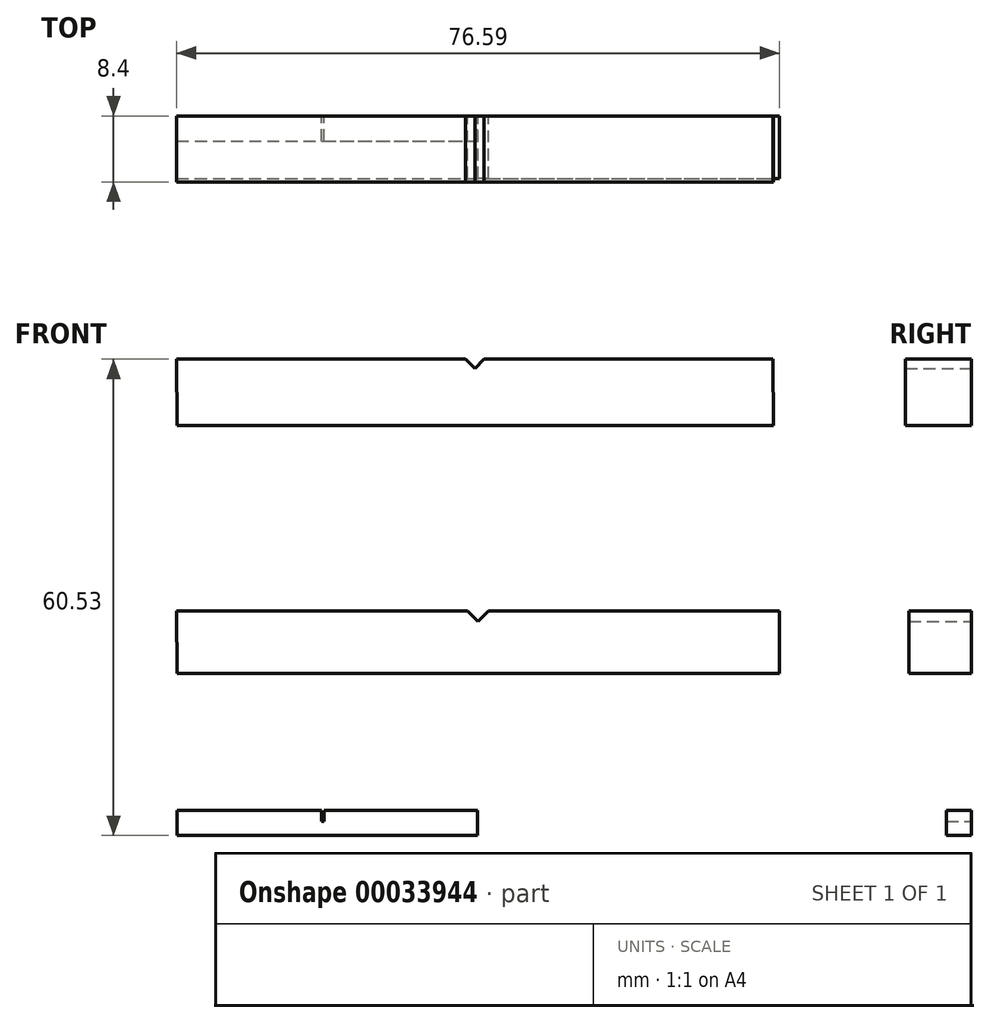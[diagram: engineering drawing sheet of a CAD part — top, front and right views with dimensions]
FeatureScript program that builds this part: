
annotation { "Feature Type Name" : "Feature", "Feature Type Description" : "" }
export const myFeature = defineFeature(function(context is Context, id is Id, definition is map)
    precondition{}
    {
        {
            var Q0;
            Q0=qCreatedBy(makeId("Front.planeOp"),FACE);
            var sketch = newSketch(context, id + "F0", { "sketchPlane" : qUnion([Q0])});
            skLineSegment(sketch, "E0.bottom", {"start": v(0, 0) * mm, "end": v(38.2, 0) * mm});
            skLineSegment(sketch, "E0.left", {"start": v(0, 0) * mm, "end": v(0, 3.2) * mm});
            skLineSegment(sketch, "E0.right", {"start": v(38.2, 0) * mm, "end": v(38.2, 3.2) * mm});
            skLineSegment(sketch, "E1", {"start": v(18.4, 1.8) * mm, "end": v(18.4, 3.2) * mm});
            skLineSegment(sketch, "E2", {"start": v(18.4, 1.8) * mm, "end": v(18.7, 1.8) * mm});
            skLineSegment(sketch, "E3", {"start": v(18.7, 1.8) * mm, "end": v(18.7, 3.2) * mm});
            skLineSegment(sketch, "E4", {"start": v(0, 3.2) * mm, "end": v(18.4, 3.2) * mm});
            skLineSegment(sketch, "E5", {"start": v(18.7, 3.2) * mm, "end": v(38.2, 3.2) * mm});
            skSolve(sketch);
        }
        {
            var Q0;
            Q0 = qSketchRegion(id + "F0", true);
            extrude(context, id + "F1", {"entities" : qUnion([Q0]), "depth" : 3.2 * mm});
        }
        {
            var Q0;
            Q0=qCreatedBy(makeId("Front.planeOp"),FACE);
            var sketch = newSketch(context, id + "F2", { "sketchPlane" : qUnion([Q0])});
            skLineSegment(sketch, "E6.bottom", {"start": v(0, 20.6) * mm, "end": v(76.55, 20.6) * mm});
            skLineSegment(sketch, "E6.left", {"start": v(0, 20.6) * mm, "end": v(-0.04, 28.55) * mm});
            skLineSegment(sketch, "E6.right", {"start": v(76.55, 20.6) * mm, "end": v(76.51, 28.55) * mm});
            skPoint(sketch, "E7", {"position": v(38.28, 20.6) * mm});
            skLineSegment(sketch, "E8", {"start": v(36.89, 28.55) * mm, "end": v(38.28, 27.2) * mm});
            skLineSegment(sketch, "E9", {"start": v(39.59, 28.55) * mm, "end": v(38.28, 27.2) * mm});
            skPoint(sketch, "E10", {"position": v(36.89, 28.55) * mm});
            skLineSegment(sketch, "E11", {"start": v(-0.04, 28.55) * mm, "end": v(36.89, 28.55) * mm});
            skLineSegment(sketch, "E12", {"start": v(39.59, 28.55) * mm, "end": v(76.51, 28.55) * mm});
            skSolve(sketch);
        }
        {
            var Q0;
            Q0=makeQuery(id+"F2.imprint","IMPRINT",FACE,{"disambiguationData":[TD([[makeQuery(id+"F2.imprint","IMPRINT",EDGE,{"derivedFrom":sQuery(id+"F2.wireOp",EDGE,"E6.bottom")}),1.0]])]});
            extrude(context, id + "F3", {"entities" : qUnion([Q0]), "depth" : 7.95 * mm});
        }
        {
            var Q0;
            Q0=qCreatedBy(makeId("Front.planeOp"),FACE);
            var sketch = newSketch(context, id + "F4", { "sketchPlane" : qUnion([Q0])});
            skLineSegment(sketch, "E13.bottom", {"start": v(0, 52.13) * mm, "end": v(75.75, 52.13) * mm});
            skLineSegment(sketch, "E13.left", {"start": v(0, 52.13) * mm, "end": v(-0.03, 60.53) * mm});
            skLineSegment(sketch, "E13.right", {"start": v(75.75, 52.13) * mm, "end": v(75.72, 60.53) * mm});
            skPoint(sketch, "E14", {"position": v(37.88, 52.13) * mm});
            skLineSegment(sketch, "E15", {"start": v(36.64, 60.53) * mm, "end": v(37.85, 59.33) * mm});
            skLineSegment(sketch, "E16", {"start": v(37.85, 59.33) * mm, "end": v(39.04, 60.53) * mm});
            skLineSegment(sketch, "E17", {"start": v(-0.03, 60.53) * mm, "end": v(36.64, 60.53) * mm});
            skLineSegment(sketch, "E18", {"start": v(39.04, 60.53) * mm, "end": v(75.72, 60.53) * mm});
            skSolve(sketch);
        }
        {
            var Q0;
            Q0=makeQuery(id+"F4.imprint","IMPRINT",FACE,{"disambiguationData":[TD([[makeQuery(id+"F4.imprint","IMPRINT",EDGE,{"derivedFrom":sQuery(id+"F4.wireOp",EDGE,"E13.bottom")}),1.0]])]});
            extrude(context, id + "F5", {"entities" : qUnion([Q0]), "depth" : 8.4 * mm});
        }
    });
